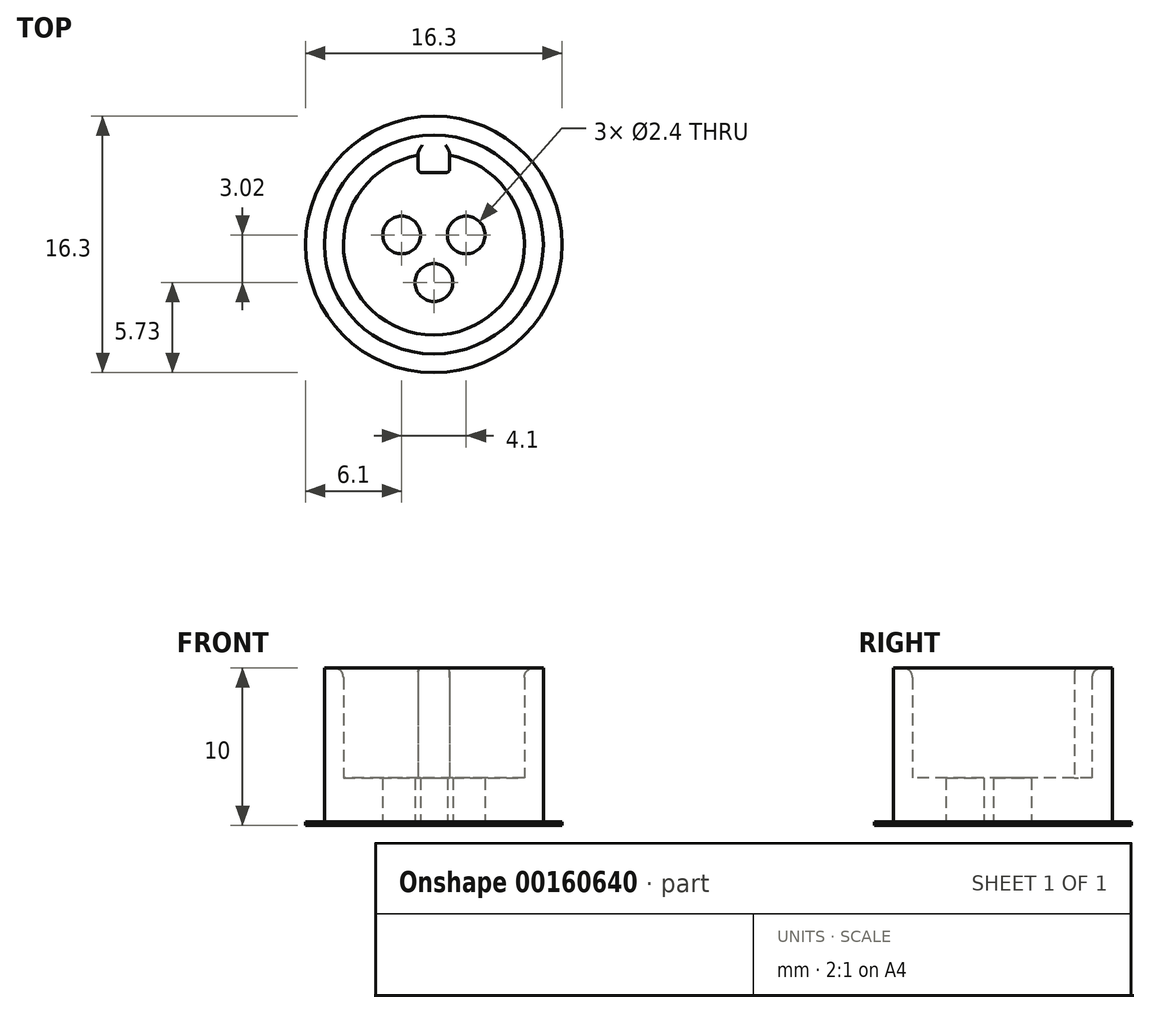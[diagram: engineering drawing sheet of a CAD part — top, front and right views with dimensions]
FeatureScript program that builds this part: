
annotation { "Feature Type Name" : "Feature", "Feature Type Description" : "" }
export const myFeature = defineFeature(function(context is Context, id is Id, definition is map)
    precondition{}
    {
        {
            var Q0;
            Q0=qCreatedBy(makeId("Top.planeOp"),FACE);
            var sketch = newSketch(context, id + "F0", { "sketchPlane" : qUnion([Q0])});
            skCircle(sketch, "E0", {"center": v(0, 0) * mm, "radius": 5.75 * mm});
            skLineSegment(sketch, "E1.bottom", {"start": v(-1, 5.75) * mm, "end": v(1, 5.75) * mm, "construction": true});
            skLineSegment(sketch, "E1.top", {"start": v(-1, 4.55) * mm, "end": v(1, 4.55) * mm});
            skLineSegment(sketch, "E1.left", {"start": v(-1, 5.75) * mm, "end": v(-1, 4.55) * mm});
            skLineSegment(sketch, "E1.right", {"start": v(1, 5.75) * mm, "end": v(1, 4.55) * mm});
            skCircle(sketch, "E2", {"center": v(0, 0) * mm, "radius": 6.95 * mm});
            skLineSegment(sketch, "E3", {"start": v(5.75, 0) * mm, "end": v(6.95, 0) * mm, "construction": true});
            skLineSegment(sketch, "E4", {"start": v(-2.05, 0.6) * mm, "end": v(2.05, 0.6) * mm, "construction": true});
            skLineSegment(sketch, "E5", {"start": v(-2.05, 0.6) * mm, "end": v(0, -2.42) * mm, "construction": true});
            skLineSegment(sketch, "E6", {"start": v(2.05, 0.6) * mm, "end": v(0, -2.42) * mm, "construction": true});
            skCircle(sketch, "E7", {"center": v(-2.05, 0.6) * mm, "radius": 1.2 * mm});
            skCircle(sketch, "E8", {"center": v(2.05, 0.6) * mm, "radius": 1.2 * mm});
            skCircle(sketch, "E9", {"center": v(0, -2.42) * mm, "radius": 1.2 * mm});
            skSolve(sketch);
        }
        {
            var Q0;
            {var subQ1=sQuery(id+"F0.wireOp",EDGE,"E1.top");Q0=makeQuery(id+"F0.imprint","IMPRINT",FACE,{"disambiguationData":[TD([[makeQuery(id+"F0.imprint","IMPRINT",EDGE,{"derivedFrom":subQ1}),-1.0]])]});}
            extrude(context, id + "F1", {"entities" : qUnion([Q0]), "depth" : 3 * mm});
        }
        {
            var Q0;
            Q0=makeQuery(id+"F0.imprint","IMPRINT",FACE,{"disambiguationData":[TD([[makeQuery(id+"F0.imprint","IMPRINT",EDGE,{"derivedFrom":sQuery(id+"F0.wireOp",EDGE,"E2")}),1.0]])]});
            var Q1;
            {var subQ5=sQuery(id+"F0.wireOp",EDGE,"E1.top");Q1=makeQuery(id+"F0.imprint","IMPRINT",FACE,{"disambiguationData":[TD([[makeQuery(id+"F0.imprint","IMPRINT",EDGE,{"derivedFrom":subQ5}),1.0]])]});}
            extrude(context, id + "F2", {"entities" : qUnion([Q0, Q1]), "operationType" : NewBodyOperationType.ADD, "depth" : (3 + 7) * mm});
        }
        {
            var Q0;
            Q0=qCreatedBy(makeId("Top.planeOp"),FACE);
            var sketch = newSketch(context, id + "F3", { "sketchPlane" : qUnion([Q0])});
            skCircle(sketch, "E10.0", {"center": v(0, 0) * mm, "radius": 6.95 * mm, "construction": true});
            skCircle(sketch, "E11", {"center": v(0, 0) * mm, "radius": 8.15 * mm});
            skLineSegment(sketch, "E12", {"start": v(6.95, 0) * mm, "end": v(8.15, 0) * mm, "construction": true});
            skCircle(sketch, "E13.0", {"center": v(-2.05, 0.6) * mm, "radius": 1.2 * mm});
            skCircle(sketch, "E14.0", {"center": v(2.05, 0.6) * mm, "radius": 1.2 * mm});
            skCircle(sketch, "E15.0", {"center": v(0, -2.42) * mm, "radius": 1.2 * mm});
            skSolve(sketch);
        }
        {
            var Q0;
            Q0=makeQuery(id+"F2.opExtrude","SWEPT_EDGE",EDGE,{"disambiguationData":[OSD([sQuery(id+"F0.wireOp",EDGE,"E1.top"),sQuery(id+"F0.wireOp",EDGE,"E1.left")])]});
            var Q1;
            Q1=makeQuery(id+"F2.opExtrude","SWEPT_EDGE",EDGE,{"disambiguationData":[OSD([sQuery(id+"F0.wireOp",EDGE,"E1.top"),sQuery(id+"F0.wireOp",EDGE,"E1.right")])]});
            var Q2;
            Q2=makeQuery(id+"F2.opExtrude","CAP_EDGE",EDGE,{"disambiguationData":[OSD([sQuery(id+"F0.wireOp",EDGE,"E1.top")])],"isStart":false});
            var Q3;
            Q3=makeQuery(id+"F2.opExtrude","CAP_EDGE",EDGE,{"disambiguationData":[OSD([sQuery(id+"F0.wireOp",EDGE,"E1.left")])],"isStart":false});
            var Q4;
            Q4=makeQuery(id+"F2.opExtrude","CAP_EDGE",EDGE,{"disambiguationData":[OSD([sQuery(id+"F0.wireOp",EDGE,"E1.right")])],"isStart":false});
            fillet(context, id + "F4", {"entities" : qUnion([Q0, Q1, Q2, Q3, Q4]), "radius" : 0.25 * mm, "allowEdgeOverflow" : false});
        }
        {
            var Q0;
            Q0=makeQuery(id+"F2.opExtrude","CAP_EDGE",EDGE,{"disambiguationData":[OSD([sQuery(id+"F0.wireOp",EDGE,"E0")])],"isStart":false});
            fillet(context, id + "F5", {"entities" : qUnion([Q0]), "radius" : 0.6 * mm, "allowEdgeOverflow" : false});
        }
        {
            var Q0;
            Q0 = qSketchRegion(id + "F3", true);
            extrude(context, id + "F6", {"entities" : qUnion([Q0]), "operationType" : NewBodyOperationType.ADD, "depth" : .2064 * mm});
        }
    });
